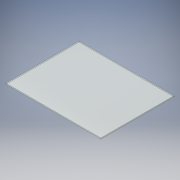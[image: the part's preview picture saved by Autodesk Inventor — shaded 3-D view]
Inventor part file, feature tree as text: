
AUTODESK INVENTOR PART (.ipt)
format: ipt  version: 2019 (Build 230136000, 136)  size: 92,672 bytes
history: native  units: mm
features: extrude x1, sketch x1
ambient origin geometry x8: Origin, YZ Plane, XZ Plane, XY Plane, X Axis, Y Axis, Z Axis, Center Point
bodies: Solid1 (feature_tree)
feature tree (2):
  extrude  "Extrusion1"  Depth=77.0mm
  sketch  "Sketch1"  dims[d0=100.0mm d1=77.0mm d2=1.0mm d3=0.0mm]
